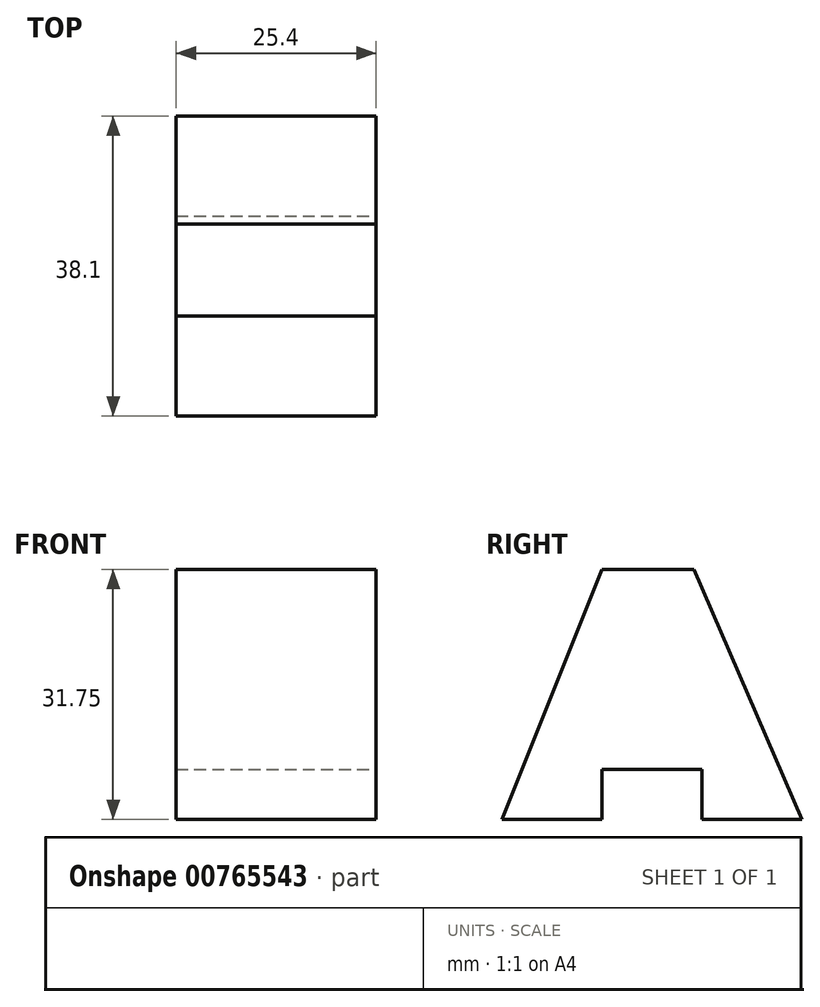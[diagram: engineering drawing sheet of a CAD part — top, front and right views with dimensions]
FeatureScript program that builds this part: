
annotation { "Feature Type Name" : "Feature", "Feature Type Description" : "" }
export const myFeature = defineFeature(function(context is Context, id is Id, definition is map)
    precondition{}
    {
        {
            var Q0;
            Q0=qCreatedBy(makeId("Right.planeOp"),FACE);
            var sketch = newSketch(context, id + "F0", { "sketchPlane" : qUnion([Q0])});
            skLineSegment(sketch, "E0", {"start": v(0, 31.75) * mm, "end": v(0, 0) * mm});
            skLineSegment(sketch, "E1", {"start": v(0, 0) * mm, "end": v(38.1, 0) * mm});
            skLineSegment(sketch, "E2", {"start": v(38.1, 0) * mm, "end": v(38.1, 31.75) * mm});
            skLineSegment(sketch, "E3", {"start": v(38.1, 31.75) * mm, "end": v(0, 31.75) * mm});
            skSolve(sketch);
        }
        {
            var Q0;
            Q0 = qSketchRegion(id + "F0", true);
            extrude(context, id + "F1", {"entities" : qUnion([Q0]), "depth" : 25.4 * mm, "offsetDistance" : 25.4 * mm});
        }
        {
            var Q0;
            Q0=makeQuery(id+"F1.opExtrude","CAP_FACE",FACE,{"disambiguationData":[OSD([sQuery(id+"F0.wireOp",EDGE,"E0"),sQuery(id+"F0.wireOp",EDGE,"E1"),sQuery(id+"F0.wireOp",EDGE,"E2"),sQuery(id+"F0.wireOp",EDGE,"E3")])],"isStart":false});
            var sketch = newSketch(context, id + "F2", { "sketchPlane" : qUnion([Q0])});
            skLineSegment(sketch, "E4", {"start": v(11.7, 31.75) * mm, "end": v(0, 0) * mm});
            skLineSegment(sketch, "E5", {"start": v(24.4, 31.75) * mm, "end": v(38.1, 0) * mm});
            skLineSegment(sketch, "E6", {"start": v(11.7, 31.75) * mm, "end": v(24.4, 31.75) * mm});
            skSolve(sketch);
        }
        {
            var Q0;
            Q0 = qSketchRegion(id + "F2", true);
            var Q1;
            {var subQ0=sQuery(id+"F2.wireOp",EDGE,"E5");Q1=makeQuery(id+"F2.imprint","IMPRINT",FACE,{"disambiguationData":[TD([[makeQuery(id+"F2.imprint","IMPRINT",EDGE,{"derivedFrom":subQ0}),1.0]])]});}
            extrude(context, id + "F3", {"entities" : qUnion([Q0, Q1]), "operationType" : NewBodyOperationType.REMOVE, "oppositeDirection" : true, "depth" : 25.4 * mm, "offsetDistance" : 25.4 * mm});
        }
        {
            var Q0;
            Q0=makeQuery(id+"F1.opExtrude","CAP_FACE",FACE,{"disambiguationData":[OSD([sQuery(id+"F0.wireOp",EDGE,"E0"),sQuery(id+"F0.wireOp",EDGE,"E1"),sQuery(id+"F0.wireOp",EDGE,"E2"),sQuery(id+"F0.wireOp",EDGE,"E3")])],"isStart":false});
            var sketch = newSketch(context, id + "F4", { "sketchPlane" : qUnion([Q0])});
            skLineSegment(sketch, "E7", {"start": v(0, 0) * mm, "end": v(12.7, 31.75) * mm});
            skLineSegment(sketch, "E8", {"start": v(12.7, 31.75) * mm, "end": v(0, 31.75) * mm});
            skSolve(sketch);
        }
        {
            var Q0;
            Q0=makeQuery(id+"F4.imprint","IMPRINT",FACE,{"disambiguationData":[TD([[makeQuery(id+"F4.imprint","IMPRINT",EDGE,{"derivedFrom":sQuery(id+"F4.wireOp",EDGE,"E7")}),1.0]])]});
            extrude(context, id + "F5", {"entities" : qUnion([Q0]), "operationType" : NewBodyOperationType.REMOVE, "endBound" : BoundingType.THROUGH_ALL, "oppositeDirection" : true, "depth" : 25.4 * mm, "offsetDistance" : 25.4 * mm});
        }
        {
            var Q0;
            Q0=makeQuery(id+"F1.opExtrude","CAP_FACE",FACE,{"disambiguationData":[OSD([sQuery(id+"F0.wireOp",EDGE,"E0"),sQuery(id+"F0.wireOp",EDGE,"E1"),sQuery(id+"F0.wireOp",EDGE,"E2"),sQuery(id+"F0.wireOp",EDGE,"E3")])],"isStart":false});
            var sketch = newSketch(context, id + "F6", { "sketchPlane" : qUnion([Q0])});
            skLineSegment(sketch, "E9", {"start": v(0, 0) * mm, "end": v(12.7, 0) * mm});
            skLineSegment(sketch, "E10", {"start": v(12.7, 0) * mm, "end": v(12.7, 6.35) * mm});
            skLineSegment(sketch, "E11", {"start": v(12.7, 6.35) * mm, "end": v(25.4, 6.35) * mm});
            skLineSegment(sketch, "E12", {"start": v(25.4, 6.35) * mm, "end": v(25.4, 0) * mm});
            skSolve(sketch);
        }
        {
            var Q0;
            {var subQ0=sQuery(id+"F6.wireOp",EDGE,"E10");Q0=makeQuery(id+"F6.imprint","IMPRINT",FACE,{"disambiguationData":[TD([[makeQuery(id+"F6.imprint","IMPRINT",EDGE,{"derivedFrom":subQ0}),-1.0]])]});}
            extrude(context, id + "F7", {"entities" : qUnion([Q0]), "operationType" : NewBodyOperationType.REMOVE, "endBound" : BoundingType.THROUGH_ALL, "oppositeDirection" : true, "depth" : 25.4 * mm, "offsetDistance" : 25.4 * mm});
        }
    });
